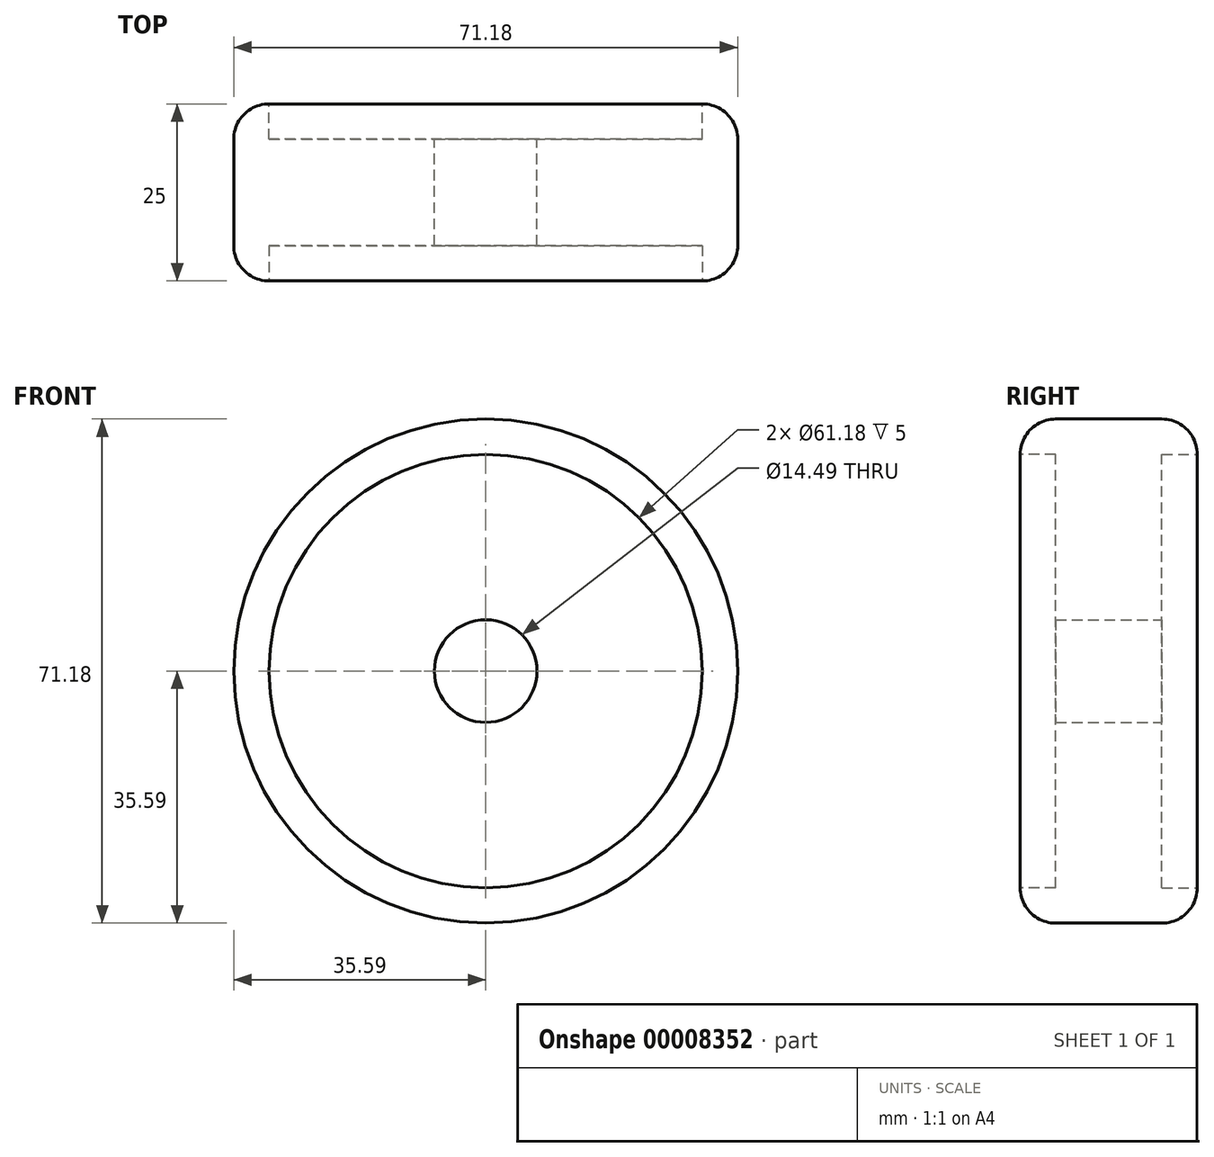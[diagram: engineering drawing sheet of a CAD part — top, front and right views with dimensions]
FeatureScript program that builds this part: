
annotation { "Feature Type Name" : "Feature", "Feature Type Description" : "" }
export const myFeature = defineFeature(function(context is Context, id is Id, definition is map)
    precondition{}
    {
        {
            var Q0;
            Q0=qCreatedBy(makeId("Front.planeOp"),FACE);
            var sketch = newSketch(context, id + "F0", { "sketchPlane" : qUnion([Q0])});
            skCircle(sketch, "E0", {"center": v(0, 0) * mm, "radius": 53.38 * mm});
            skSolve(sketch);
        }
        {
            var Q0;
            Q0=makeQuery(id+"F0.imprint","IMPRINT",FACE,{"disambiguationData":[TD([[makeQuery(id+"F0.imprint","IMPRINT",EDGE,{"derivedFrom":sQuery(id+"F0.wireOp",EDGE,"E0")}),1.0]])]});
            extrude(context, id + "F1", {"entities" : qUnion([Q0]), "depth" : 90 * mm});
        }
        {
            var Q0;
            Q0=makeQuery(id+"F1.opExtrude","CAP_FACE",FACE,{"disambiguationData":[OSD([sQuery(id+"F0.wireOp",EDGE,"E0")])],"isStart":false});
            shell(context, id + "F2", {"entities" : qUnion([Q0]), "thickness" : 5 * mm});
        }
        {
            var Q0;
            Q0=qCreatedBy(makeId("Front.planeOp"),FACE);
            var sketch = newSketch(context, id + "F3", { "sketchPlane" : qUnion([Q0])});
            skCircle(sketch, "E1", {"center": v(0, 0) * mm, "radius": 16.47 * mm});
            skSolve(sketch);
        }
        {
            var Q0;
            Q0=makeQuery(id+"F3.imprint","IMPRINT",FACE,{"disambiguationData":[TD([[makeQuery(id+"F3.imprint","IMPRINT",EDGE,{"derivedFrom":sQuery(id+"F3.wireOp",EDGE,"E1")}),1.0]])]});
            extrude(context, id + "F4", {"entities" : qUnion([Q0]), "operationType" : NewBodyOperationType.ADD, "depth" : 0.5 * mm});
        }
        {
            var Q0;
            Q0=makeQuery(id+"F1.opExtrude","CAP_FACE",FACE,{"disambiguationData":[OSD([sQuery(id+"F0.wireOp",EDGE,"E0")])],"isStart":true});
            var sketch = newSketch(context, id + "F5", { "sketchPlane" : qUnion([Q0])});
            skCircle(sketch, "E2", {"center": v(0, 0) * mm, "radius": 18.77 * mm});
            skSolve(sketch);
        }
        {
            var Q0;
            Q0=makeQuery(id+"F5.imprint","IMPRINT",FACE,{"disambiguationData":[TD([[makeQuery(id+"F5.imprint","IMPRINT",EDGE,{"derivedFrom":sQuery(id+"F5.wireOp",EDGE,"E2")}),1.0]])]});
            extrude(context, id + "F6", {"entities" : qUnion([Q0]), "operationType" : NewBodyOperationType.ADD, "oppositeDirection" : true, "depth" : 0.5 * mm});
        }
        {
            var Q0;
            Q0 = qSketchRegion(id + "F3", true);
            extrude(context, id + "F7", {"entities" : qUnion([Q0]), "operationType" : NewBodyOperationType.ADD, "depth" : 4 * mm});
        }
        {
            var Q0;
            {var subQ0=sQuery(id+"F0.wireOp",EDGE,"E0");Q0=makeQuery(id+"F2.opShell","OFFSET_FACE",FACE,{"disambiguationData":[OSD([subQ0]),TDD([makeQuery(id+"F1.opExtrude","CAP_FACE",FACE,{"disambiguationData":[OSD([subQ0])],"isStart":true})])]});}
            var sketch = newSketch(context, id + "F8", { "sketchPlane" : qUnion([Q0])});
            skCircle(sketch, "E3", {"center": v(0, 0) * mm, "radius": 26.79 * mm});
            skSolve(sketch);
        }
        {
            var Q0;
            Q0=makeQuery(id+"F8.imprint","IMPRINT",FACE,{"disambiguationData":[TD([[makeQuery(id+"F8.imprint","IMPRINT",EDGE,{"derivedFrom":sQuery(id+"F8.wireOp",EDGE,"E3")}),1.0]])]});
            extrude(context, id + "F9", {"entities" : qUnion([Q0]), "operationType" : NewBodyOperationType.ADD, "depth" : 10 * mm});
        }
        {
            var Q0;
            Q0=makeQuery(id+"F9.opExtrude","CAP_FACE",FACE,{"disambiguationData":[OSD([sQuery(id+"F8.wireOp",EDGE,"E3")])],"isStart":false});
            fillet(context, id + "F10", {"entities" : qUnion([Q0]), "radius" : 5 * mm, "tangentPropagation" : true, "allowEdgeOverflow" : false});
        }
        {
            var Q0;
            {var subQ0=sQuery(id+"F0.wireOp",EDGE,"E0");Q0=makeQuery(id+"F2.opShell","OFFSET_FACE",FACE,{"disambiguationData":[OSD([subQ0]),TDD([makeQuery(id+"F1.opExtrude","CAP_FACE",FACE,{"disambiguationData":[OSD([subQ0])],"isStart":true})])]});}
            fillet(context, id + "F11", {"entities" : qUnion([Q0]), "radius" : 5 * mm, "tangentPropagation" : true, "allowEdgeOverflow" : false});
        }
        {
            var Q0;
            Q0=makeQuery(id+"F1.opExtrude","CAP_EDGE",EDGE,{"disambiguationData":[OSD([sQuery(id+"F0.wireOp",EDGE,"E0")])],"isStart":false});
            chamfer(context, id + "F12", {"entities" : qUnion([Q0]), "width" : 10 * mm, "tangentPropagation" : true});
        }
        {
            var Q0;
            Q0=makeQuery(id+"F1.opExtrude","CAP_FACE",FACE,{"disambiguationData":[OSD([sQuery(id+"F0.wireOp",EDGE,"E0")])],"isStart":true});
            var sketch = newSketch(context, id + "F13", { "sketchPlane" : qUnion([Q0])});
            skCircle(sketch, "E4", {"center": v(0, 0) * mm, "radius": 25.89 * mm});
            skSolve(sketch);
        }
        {
            var Q0;
            Q0=makeQuery(id+"F13.imprint","IMPRINT",FACE,{"disambiguationData":[TD([[makeQuery(id+"F13.imprint","IMPRINT",EDGE,{"derivedFrom":sQuery(id+"F13.wireOp",EDGE,"E4")}),1.0]])]});
            extrude(context, id + "F14", {"entities" : qUnion([Q0]), "operationType" : NewBodyOperationType.ADD, "oppositeDirection" : true, "depth" : 12.77 * mm});
        }
        {
            var Q0;
            Q0 = qSketchRegion(id + "F8", true);
            extrude(context, id + "F15", {"entities" : qUnion([Q0]), "operationType" : NewBodyOperationType.ADD, "depth" : 25 * mm});
        }
        {
            var Q0;
            Q0 = qSketchRegion(id + "F8", true);
            extrude(context, id + "F16", {"entities" : qUnion([Q0]), "operationType" : NewBodyOperationType.REMOVE, "depth" : 20.78 * mm});
        }
        {
            var Q0;
            Q0 = qSketchRegion(id + "F13", true);
            extrude(context, id + "F17", {"entities" : qUnion([Q0]), "operationType" : NewBodyOperationType.REMOVE, "oppositeDirection" : true, "depth" : 5.46 * mm});
        }
        {
            var Q0;
            Q0=makeQuery(id+"F16.boolean.opBoolean","SPLIT",BODY,{"disambiguationData":[OD(0.0)],"derivedFrom":makeQuery(id+"F1.opExtrude","SWEPT_BODY",BODY,{"disambiguationData":[OSD([sQuery(id+"F0.wireOp",EDGE,"E0")])]})});
            var Q1;
            Q1=makeQuery(id+"F16.boolean.opBoolean","SPLIT",BODY,{"disambiguationData":[OD(1.0)],"derivedFrom":makeQuery(id+"F1.opExtrude","SWEPT_BODY",BODY,{"disambiguationData":[OSD([sQuery(id+"F0.wireOp",EDGE,"E0")])]})});
            deleteBodies(context, id + "F18", {"entities" : qUnion([Q0, Q1])});
        }
        {
            var Q0;
            Q0=qCreatedBy(makeId("Front.planeOp"),FACE);
            var sketch = newSketch(context, id + "F19", { "sketchPlane" : qUnion([Q0])});
            skCircle(sketch, "E5", {"center": v(0, 0) * mm, "radius": 35.6 * mm});
            skSolve(sketch);
        }
        {
            var Q0;
            Q0=makeQuery(id+"F19.imprint","IMPRINT",FACE,{"disambiguationData":[TD([[makeQuery(id+"F19.imprint","IMPRINT",EDGE,{"derivedFrom":sQuery(id+"F19.wireOp",EDGE,"E5")}),1.0]])]});
            extrude(context, id + "F20", {"entities" : qUnion([Q0]), "depth" : 25 * mm});
        }
        {
            var Q0;
            Q0=makeQuery(id+"F20.opExtrude","CAP_FACE",FACE,{"disambiguationData":[OSD([sQuery(id+"F19.wireOp",EDGE,"E5")])],"isStart":false});
            var Q1;
            Q1=makeQuery(id+"F20.opExtrude","CAP_EDGE",EDGE,{"disambiguationData":[OSD([sQuery(id+"F19.wireOp",EDGE,"E5")])],"isStart":true});
            var Q2;
            Q2=makeQuery(id+"F20.opExtrude","SWEPT_FACE",FACE,{"disambiguationData":[OSD([sQuery(id+"F19.wireOp",EDGE,"E5")])]});
            fillet(context, id + "F21", {"entities" : qUnion([Q0, Q1, Q2]), "radius" : 5 * mm, "tangentPropagation" : true, "allowEdgeOverflow" : false});
        }
        {
            var Q0;
            Q0=makeQuery(id+"F20.opExtrude","CAP_FACE",FACE,{"disambiguationData":[OSD([sQuery(id+"F19.wireOp",EDGE,"E5")])],"isStart":true});
            extrude(context, id + "F22", {"entities" : qUnion([Q0]), "operationType" : NewBodyOperationType.REMOVE, "oppositeDirection" : true, "depth" : 5 * mm});
        }
        {
            var Q0;
            Q0=makeQuery(id+"F20.opExtrude","CAP_FACE",FACE,{"disambiguationData":[OSD([sQuery(id+"F19.wireOp",EDGE,"E5")])],"isStart":false});
            extrude(context, id + "F23", {"entities" : qUnion([Q0]), "operationType" : NewBodyOperationType.REMOVE, "oppositeDirection" : true, "depth" : 5 * mm});
        }
        {
            var Q0;
            Q0=makeQuery(id+"F22.boolean.opBoolean","COPY",FACE,{"derivedFrom":makeQuery(id+"F22.opExtrude","CAP_FACE",FACE,{"disambiguationData":[OSD([sQuery(id+"F19.wireOp",EDGE,"E5")])],"isStart":false})});
            var sketch = newSketch(context, id + "F24", { "sketchPlane" : qUnion([Q0])});
            skCircle(sketch, "E6", {"center": v(0, 0) * mm, "radius": 7.24 * mm});
            skSolve(sketch);
        }
        {
            var Q0;
            Q0=makeQuery(id+"F24.imprint","IMPRINT",FACE,{"disambiguationData":[TD([[makeQuery(id+"F24.imprint","IMPRINT",EDGE,{"derivedFrom":sQuery(id+"F24.wireOp",EDGE,"E6")}),1.0]])]});
            extrude(context, id + "F25", {"entities" : qUnion([Q0]), "operationType" : NewBodyOperationType.REMOVE, "oppositeDirection" : true, "depth" : 15 * mm});
        }
    });
